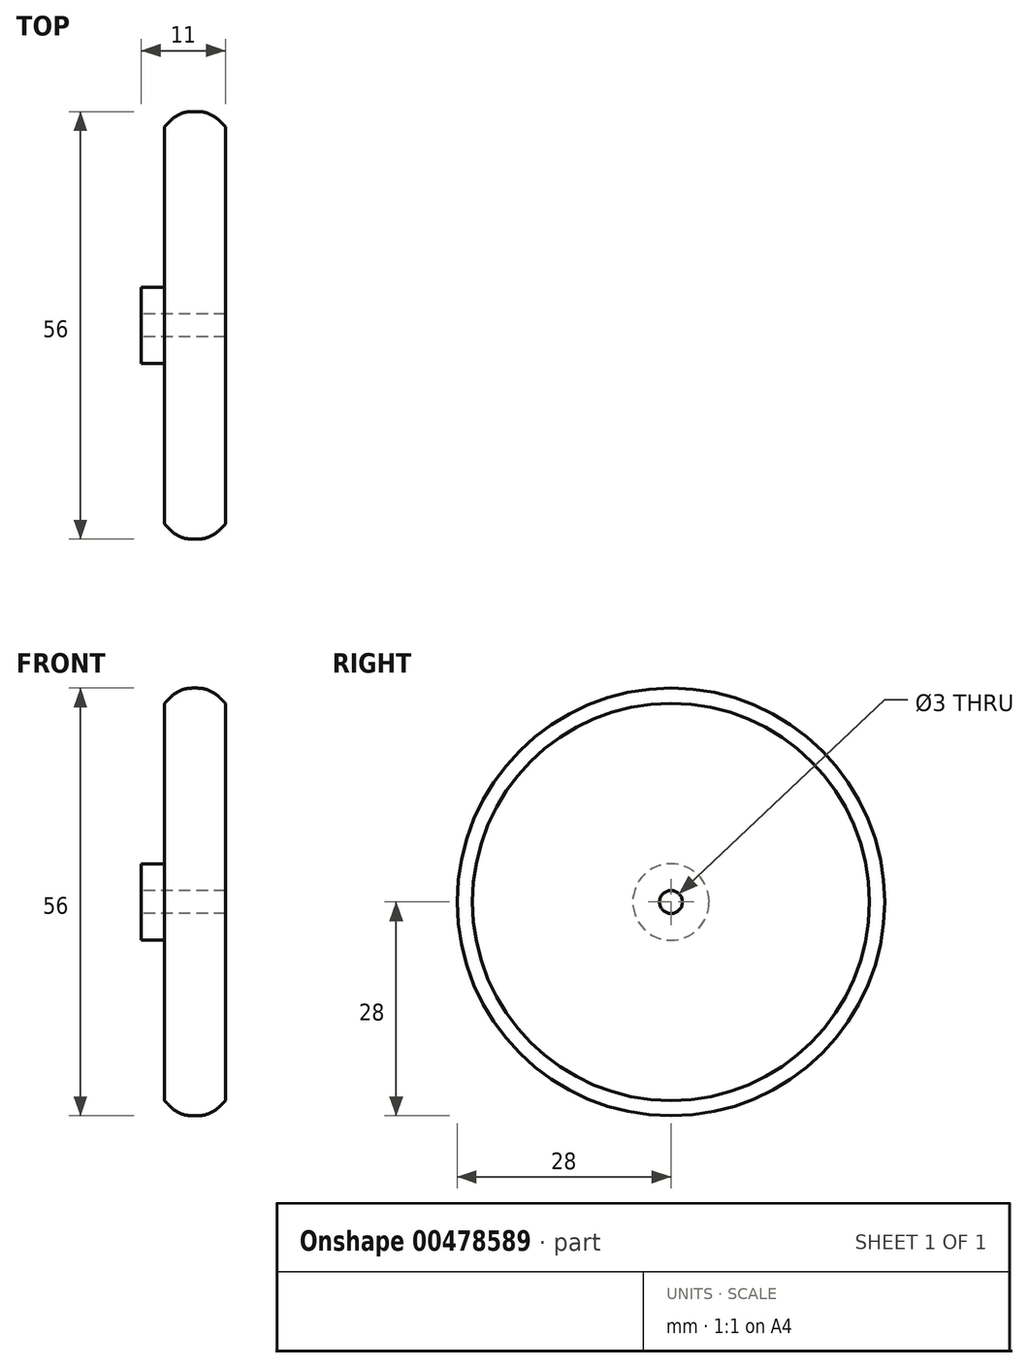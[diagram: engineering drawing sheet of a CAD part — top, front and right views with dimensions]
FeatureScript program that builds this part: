
annotation { "Feature Type Name" : "Feature", "Feature Type Description" : "" }
export const myFeature = defineFeature(function(context is Context, id is Id, definition is map)
    precondition{}
    {
        {
            var Q0;
            Q0=qCreatedBy(makeId("Top.planeOp"),FACE);
            var sketch = newSketch(context, id + "F0", { "sketchPlane" : qUnion([Q0])});
            skLineSegment(sketch, "E0", {"start": v(0, 0) * mm, "end": v(0, 5) * mm});
            skLineSegment(sketch, "E1", {"start": v(0, 5) * mm, "end": v(3, 5) * mm});
            skLineSegment(sketch, "E2", {"start": v(3, 5) * mm, "end": v(3, 25) * mm});
            skLineSegment(sketch, "E3", {"start": v(3, 25) * mm, "end": v(5, 25) * mm});
            skLineSegment(sketch, "E4", {"start": v(5, 25) * mm, "end": v(5, 28) * mm});
            skLineSegment(sketch, "E5", {"start": v(5, 28) * mm, "end": v(9, 28) * mm});
            skLineSegment(sketch, "E6", {"start": v(9, 28) * mm, "end": v(9, 25) * mm});
            skLineSegment(sketch, "E7", {"start": v(9, 25) * mm, "end": v(11, 25) * mm});
            skLineSegment(sketch, "E8", {"start": v(11, 25) * mm, "end": v(11, 0) * mm});
            skLineSegment(sketch, "E9", {"start": v(0, 0) * mm, "end": v(11, 0) * mm});
            skSolve(sketch);
        }
        {
            var Q0;
            Q0 = qSketchRegion(id + "F0", true);
            var Q1;
            Q1=sQuery(id+"F0.wireOp",EDGE,"E9");
            revolve(context, id + "F1", {"entities" : qUnion([Q0]), "axis" : qUnion([Q1]), "revolveType" : RevolveType.FULL});
        }
        {
            var Q0;
            Q0=makeQuery(id+"F1.opRevolve","SWEPT_FACE",FACE,{"disambiguationData":[OSD([sQuery(id+"F0.wireOp",EDGE,"E0")])]});
            var sketch = newSketch(context, id + "F2", { "sketchPlane" : qUnion([Q0])});
            skCircle(sketch, "E10", {"center": v(0, 0) * mm, "radius": 1.5 * mm});
            skSolve(sketch);
        }
        {
            var Q0;
            Q0 = qSketchRegion(id + "F2", true);
            extrude(context, id + "F3", {"entities" : qUnion([Q0]), "operationType" : NewBodyOperationType.REMOVE, "oppositeDirection" : true, "depth" : 25 * mm});
        }
        {
            var Q0;
            Q0=qCreatedBy(makeId("Top.planeOp"),FACE);
            var sketch = newSketch(context, id + "F4", { "sketchPlane" : qUnion([Q0])});
            skArc(sketch, "E11", {"start": v(10.7, 25) * mm, "mid": v(7.07, 30) * mm, "end": v(3.44, 25) * mm});
            skLineSegment(sketch, "E12", {"start": v(5, 28) * mm, "end": v(9.15, 28) * mm, "construction": true});
            skLineSegment(sketch, "E13", {"start": v(7.07, 26.18) * mm, "end": v(7.07, 28) * mm, "construction": true});
            skLineSegment(sketch, "E14", {"start": v(3, 25) * mm, "end": v(5, 25) * mm, "construction": true});
            skLineSegment(sketch, "E15", {"start": v(9, 25) * mm, "end": v(11, 25) * mm, "construction": true});
            skLineSegment(sketch, "E16", {"start": v(7.07, 30) * mm, "end": v(0, 30) * mm, "construction": true});
            skLineSegment(sketch, "E17", {"start": v(0, 30) * mm, "end": v(0, 0) * mm, "construction": true});
            skLineSegment(sketch, "E18", {"start": v(3.44, 25) * mm, "end": v(10.7, 25) * mm});
            skSolve(sketch);
        }
        {
            var Q0;
            Q0=qCreatedBy(makeId("Top.planeOp"),FACE);
            var sketch = newSketch(context, id + "F5", { "sketchPlane" : qUnion([Q0])});
            skLineSegment(sketch, "E19", {"start": v(9, 25) * mm, "end": v(11, 25) * mm, "construction": true});
            skLineSegment(sketch, "E20", {"start": v(5, 28) * mm, "end": v(9, 28) * mm, "construction": true});
            skLineSegment(sketch, "E21", {"start": v(3, 25) * mm, "end": v(5, 25) * mm, "construction": true});
            skLineSegment(sketch, "E22", {"start": v(11, 25) * mm, "end": v(11, 26) * mm});
            skLineSegment(sketch, "E23", {"start": v(11, 26) * mm, "end": v(9, 28) * mm});
            skLineSegment(sketch, "E24", {"start": v(9, 28) * mm, "end": v(5, 28) * mm});
            skLineSegment(sketch, "E25", {"start": v(5, 28) * mm, "end": v(3, 26) * mm});
            skLineSegment(sketch, "E26", {"start": v(3, 26) * mm, "end": v(3, 25) * mm});
            skLineSegment(sketch, "E27.0", {"start": v(11, -25) * mm, "end": v(11, 25) * mm, "construction": true});
            skLineSegment(sketch, "E28.0", {"start": v(3, -25) * mm, "end": v(3, 25) * mm, "construction": true});
            skLineSegment(sketch, "E29", {"start": v(3, 25) * mm, "end": v(11, 25) * mm});
            skLineSegment(sketch, "E30.0", {"start": v(5, -28) * mm, "end": v(5, 28) * mm, "construction": true});
            skLineSegment(sketch, "E31.0", {"start": v(9, -28) * mm, "end": v(9, 28) * mm, "construction": true});
            skSolve(sketch);
        }
        {
            var Q0;
            Q0=makeQuery(id+"F5.imprint","IMPRINT",FACE,{"disambiguationData":[TD([[makeQuery(id+"F5.imprint","IMPRINT",EDGE,{"derivedFrom":sQuery(id+"F5.wireOp",EDGE,"E22")}),1.0]])]});
            var Q1;
            Q1=makeQuery(id+"F3.boolean.opBoolean","COPY",FACE,{"derivedFrom":makeQuery(id+"F3.opExtrude","SWEPT_FACE",FACE,{"disambiguationData":[OSD([sQuery(id+"F2.wireOp",EDGE,"E10")])]})});
            revolve(context, id + "F6", {"operationType" : NewBodyOperationType.ADD, "entities" : qUnion([Q0]), "axis" : qUnion([Q1]), "revolveType" : RevolveType.FULL});
        }
        {
            var Q0;
            Q0=makeQuery(id+"F6.boolean.opBoolean","MERGE",EDGE,{"derivedFrom":[makeQuery(id+"F1.opRevolve","SWEPT_EDGE",EDGE,{"disambiguationData":[OSD([sQuery(id+"F0.wireOp",EDGE,"E5"),sQuery(id+"F0.wireOp",EDGE,"E6")])]}),makeQuery(id+"F6.opRevolve","SWEPT_EDGE",EDGE,{"disambiguationData":[OSD([sQuery(id+"F5.wireOp",EDGE,"E23"),sQuery(id+"F5.wireOp",EDGE,"E24")])]})]});
            var Q1;
            Q1=makeQuery(id+"F6.boolean.opBoolean","MERGE",EDGE,{"derivedFrom":[makeQuery(id+"F1.opRevolve","SWEPT_EDGE",EDGE,{"disambiguationData":[OSD([sQuery(id+"F0.wireOp",EDGE,"E4"),sQuery(id+"F0.wireOp",EDGE,"E5")])]}),makeQuery(id+"F6.opRevolve","SWEPT_EDGE",EDGE,{"disambiguationData":[OSD([sQuery(id+"F5.wireOp",EDGE,"E24"),sQuery(id+"F5.wireOp",EDGE,"E25")])]})]});
            fillet(context, id + "F7", {"entities" : qUnion([Q0, Q1]), "radius" : 4 * mm, "tangentPropagation" : true, "allowEdgeOverflow" : false});
        }
    });
